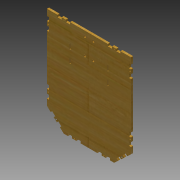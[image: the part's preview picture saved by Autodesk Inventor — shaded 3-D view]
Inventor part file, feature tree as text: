
AUTODESK INVENTOR PART (.ipt)
format: ipt  version: 2014 (Build 180170000, 170)  size: 348,672 bytes
history: native  units: mm
features: sketch x3, extrude x3, plane x2
ambient origin geometry x8: Origin, YZ Plane, XZ Plane, XY Plane, X Axis, Y Axis, Z Axis, Center Point
bodies: Body1 (feature_tree)
feature tree (8):
  sketch  "Sketch1"  dims[d41=2.5mm d326=10.0mm]
  plane  "Work Plane2"
  sketch  "Sketch2"  dims[d327=10.0mm d328=10.0mm]
  plane  "Work Plane1"
  sketch  "Sketch3"  dims[d329=5.0mm d330=5.0mm d381=5.0mm d382=10.0mm d383=10.0mm d384=5.0mm d385=10.0mm d392=5.0mm d393=10.0mm d458=35.0mm d460=20.0mm d465=10.0mm d466=3.0mm d467=10.0mm d468=3.0mm d469=10.0mm d470=3.0mm d471=10.0mm d472=3.0mm d475=40.0mm d476=5.0mm d477=5.0mm d489=3.0mm d512=3.0mm d513=3.0mm d514=3.0mm d515=3.0mm d529=15.0mm d530=10.0mm d531=5.0mm d532=5.0mm d533=10.0mm d535=200.0mm d539=37.5mm d543=2.5mm d558=5.0mm d573=10.0mm d574=140.0mm d575=110.0mm d576=30.0mm d580=15.0mm d581=3.0mm d583=5.0mm d584=10.0mm d586=5.0mm d587=10.0mm d594=120.0mm d595=10.0mm d596=5.0mm d597=10.0mm d598=10.0mm d599=10.0mm d600=3.0mm d602=5.0mm d603=10.0mm d604=10.0mm d605=10.0mm d606=3.0mm d607=5.0mm d608=0.0mm d609=5.0mm d610=0.0mm d611=40.0mm d612=25.0mm d613=70.0mm d636=200.0mm d637=37.5mm d638=237.5mm d653=5.0mm d654=10.0mm d655=10.0mm d656=10.0mm d657=5.0mm d658=2.5mm d659=3.0mm d662=5.0mm d663=90.0deg d664=10.0mm d665=10.0mm d666=10.0mm d667=5.0mm d668=2.5mm d669=3.0mm d674=5.0mm d676=12.5mm d677=5.0mm d678=0.0mm]
  extrude  "Extrusion37"  Depth=10.0mm
  extrude  "Extrusion38"  Depth=10.0mm
  extrude  "Extrusion42"  Depth=5.0mm
